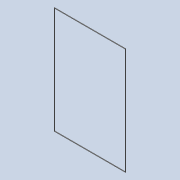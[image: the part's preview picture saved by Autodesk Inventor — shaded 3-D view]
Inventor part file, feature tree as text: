
AUTODESK INVENTOR PART (.ipt)
format: ipt  version: 2020 (Build 240168000, 168)  size: 78,848 bytes
history: native  units: mm
features: extrude x1, sketch x1
ambient origin geometry x8: Origin, YZ Plane, XZ Plane, XY Plane, X Axis, Y Axis, Z Axis, Center Point
bodies: Solid1 (feature_tree)
feature tree (2):
  extrude  "Extrusion1"  Depth=100.0mm
  sketch  "Sketch1"  dims[d0=150.0mm d1=100.0mm d2=0.6mm d3=0.6mm d4=0.0mm]
